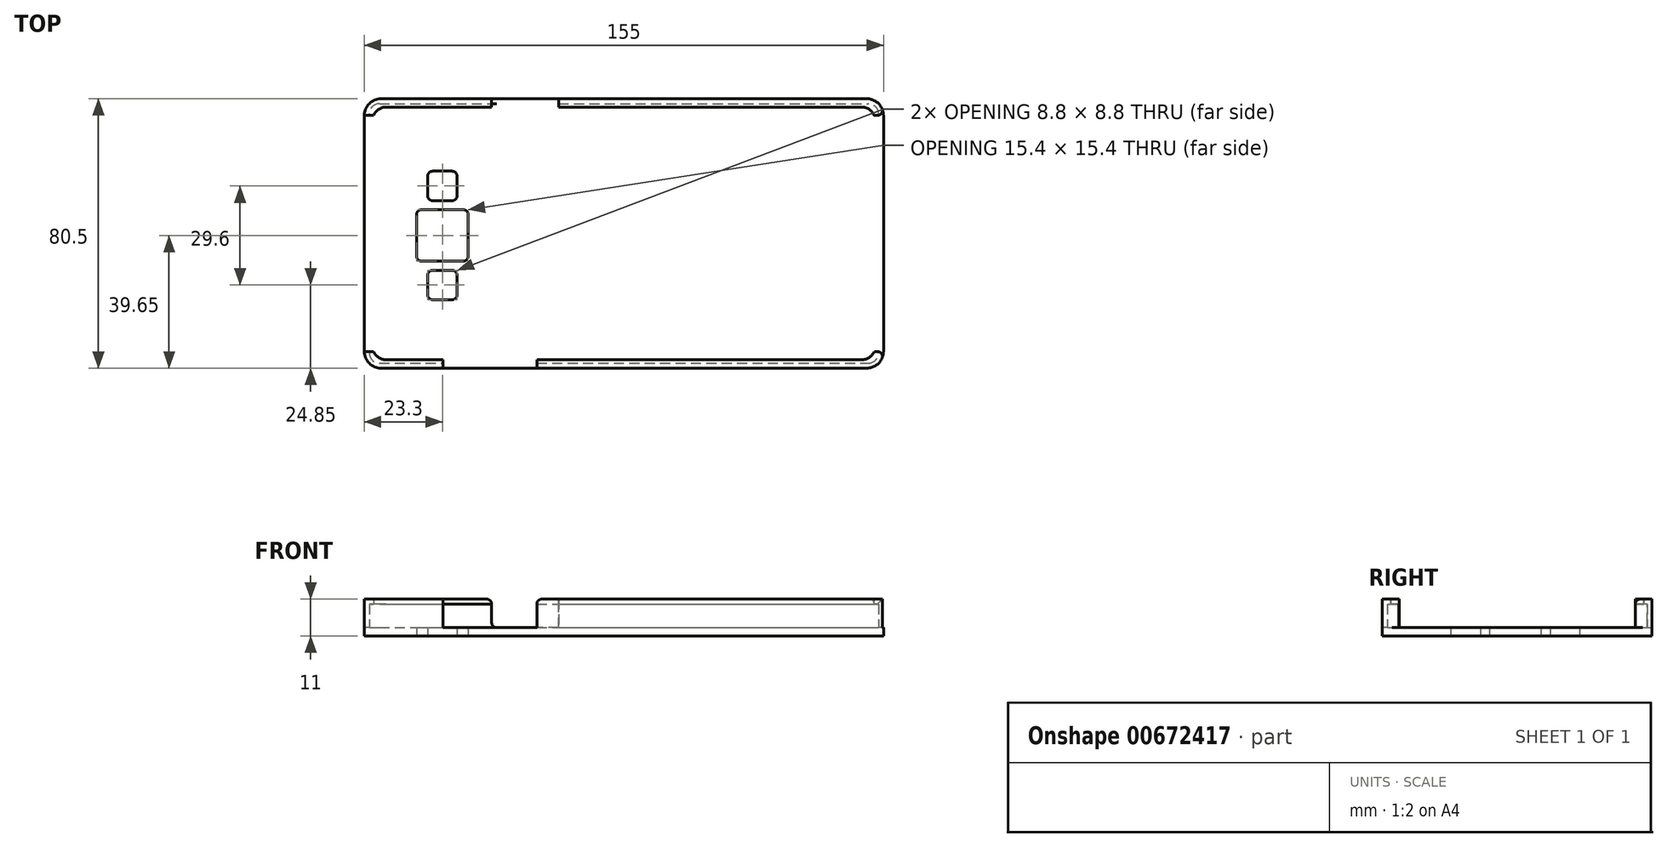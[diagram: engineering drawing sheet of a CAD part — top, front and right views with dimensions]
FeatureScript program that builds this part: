
annotation { "Feature Type Name" : "Feature", "Feature Type Description" : "" }
export const myFeature = defineFeature(function(context is Context, id is Id, definition is map)
    precondition{}
    {
        {
            var Q0;
            Q0=qCreatedBy(makeId("Top.planeOp"),FACE);
            var sketch = newSketch(context, id + "F0", { "sketchPlane" : qUnion([Q0])});
            skLineSegment(sketch, "E0.bottom", {"start": v(0, 0) * mm, "end": v(155, 0) * mm});
            skLineSegment(sketch, "E0.top", {"start": v(0, 80.5) * mm, "end": v(155, 80.5) * mm});
            skLineSegment(sketch, "E0.left", {"start": v(0, 0) * mm, "end": v(0, 80.5) * mm});
            skLineSegment(sketch, "E0.right", {"start": v(155, 0) * mm, "end": v(155, 80.5) * mm});
            skSolve(sketch);
        }
        {
            var Q0;
            Q0=qSketchRegion(id+"F0",true);
            extrude(context, id + "F1", {"entities" : qUnion([Q0]), "depth" : 9.5 * mm, "offsetDistance" : 25 * mm});
        }
        {
            var Q0;
            Q0=makeQuery(id+"F1.opExtrude","CAP_FACE",FACE,{"disambiguationData":[OSD([sQuery(id+"F0.wireOp",EDGE,"E0.bottom"),sQuery(id+"F0.wireOp",EDGE,"E0.top"),sQuery(id+"F0.wireOp",EDGE,"E0.left"),sQuery(id+"F0.wireOp",EDGE,"E0.right")])],"isStart":false});
            shell(context, id + "F2", {"entities" : qUnion([Q0]), "thickness" : 1.5 * mm});
        }
        {
            var Q0;
            Q0=makeQuery(id+"F1.opExtrude","CAP_FACE",FACE,{"disambiguationData":[OSD([sQuery(id+"F0.wireOp",EDGE,"E0.bottom"),sQuery(id+"F0.wireOp",EDGE,"E0.top"),sQuery(id+"F0.wireOp",EDGE,"E0.left"),sQuery(id+"F0.wireOp",EDGE,"E0.right")])],"isStart":false});
            var sketch = newSketch(context, id + "F3", { "sketchPlane" : qUnion([Q0])});
            skLineSegment(sketch, "E1.0", {"start": v(2.5, 78) * mm, "end": v(152.5, 78) * mm});
            skLineSegment(sketch, "E1.1", {"start": v(2.5, 2.5) * mm, "end": v(2.5, 78) * mm});
            skLineSegment(sketch, "E1.2", {"start": v(2.5, 2.5) * mm, "end": v(152.5, 2.5) * mm});
            skLineSegment(sketch, "E1.3", {"start": v(152.5, 2.5) * mm, "end": v(152.5, 78) * mm});
            skSolve(sketch);
        }
        {
            var Q0;
            Q0=makeQuery(id+"F3.imprint","IMPRINT",FACE,{"disambiguationData":[TD([[makeQuery(id+"F3.imprint","IMPRINT",EDGE,{"derivedFrom":sQuery(id+"F3.wireOp",EDGE,"E1.0")}),1.0]])]});
            var Q1;
            {var subQ6=sQuery(id+"F0.wireOp",EDGE,"E0.bottom");var subQ7=makeQuery(id+"F1.opExtrude","CAP_EDGE",EDGE,{"disambiguationData":[OSD([subQ6])],"isStart":false});Q1=makeQuery(id+"F3.imprint","IMPRINT",FACE,{"disambiguationData":[TD([[makeQuery(id+"F3.imprint","IMPRINT",EDGE,{"derivedFrom":subQ7}),1.0]])]});}
            extrude(context, id + "F4", {"entities" : qUnion([Q0, Q1]), "operationType" : NewBodyOperationType.ADD, "depth" : 1.5 * mm, "offsetDistance" : 25 * mm});
        }
        {
            var Q0;
            Q0=makeQuery(id+"F1.opExtrude","CAP_FACE",FACE,{"disambiguationData":[OSD([sQuery(id+"F0.wireOp",EDGE,"E0.bottom"),sQuery(id+"F0.wireOp",EDGE,"E0.top"),sQuery(id+"F0.wireOp",EDGE,"E0.left"),sQuery(id+"F0.wireOp",EDGE,"E0.right")])],"isStart":true});
            var sketch = newSketch(context, id + "F5", { "sketchPlane" : qUnion([Q0])});
            skLineSegment(sketch, "E2.bottom", {"start": v(18.9, -20.45) * mm, "end": v(27.7, -20.45) * mm});
            skLineSegment(sketch, "E2.top", {"start": v(18.9, -29.25) * mm, "end": v(27.7, -29.25) * mm});
            skLineSegment(sketch, "E2.left", {"start": v(18.9, -20.45) * mm, "end": v(18.9, -29.25) * mm});
            skLineSegment(sketch, "E2.right", {"start": v(27.7, -20.45) * mm, "end": v(27.7, -29.25) * mm});
            skLineSegment(sketch, "E3.bottom", {"start": v(15.6, -31.95) * mm, "end": v(31, -31.95) * mm});
            skLineSegment(sketch, "E3.top", {"start": v(15.6, -47.35) * mm, "end": v(31, -47.35) * mm});
            skLineSegment(sketch, "E3.left", {"start": v(15.6, -31.95) * mm, "end": v(15.6, -47.35) * mm});
            skLineSegment(sketch, "E3.right", {"start": v(31, -31.95) * mm, "end": v(31, -47.35) * mm});
            skLineSegment(sketch, "E4.bottom", {"start": v(18.9, -50.05) * mm, "end": v(27.7, -50.05) * mm});
            skLineSegment(sketch, "E4.top", {"start": v(18.9, -58.85) * mm, "end": v(27.7, -58.85) * mm});
            skLineSegment(sketch, "E4.left", {"start": v(18.9, -50.05) * mm, "end": v(18.9, -58.85) * mm});
            skLineSegment(sketch, "E4.right", {"start": v(27.7, -50.05) * mm, "end": v(27.7, -58.85) * mm});
            skLineSegment(sketch, "E5", {"start": v(12.52, -39.65) * mm, "end": v(41, -39.65) * mm});
            skPoint(sketch, "E5.startSnap0", {"position": v(15.6, -39.65) * mm});
            skLineSegment(sketch, "E6", {"start": v(16.62, -24.85) * mm, "end": v(34.64, -24.85) * mm});
            skPoint(sketch, "E6.startSnap0", {"position": v(18.9, -24.85) * mm});
            skLineSegment(sketch, "E7", {"start": v(16.41, -54.45) * mm, "end": v(34.85, -54.45) * mm});
            skPoint(sketch, "E7.startSnap0", {"position": v(18.9, -54.45) * mm});
            skSolve(sketch);
        }
        {
            var Q0;
            {var subQ0=sQuery(id+"F5.wireOp",EDGE,"E2.top");Q0=makeQuery(id+"F5.imprint","IMPRINT",FACE,{"disambiguationData":[TD([[makeQuery(id+"F5.imprint","IMPRINT",EDGE,{"derivedFrom":subQ0}),1.0]])]});}
            var Q1;
            {var subQ0=sQuery(id+"F5.wireOp",EDGE,"E2.bottom");Q1=makeQuery(id+"F5.imprint","IMPRINT",FACE,{"disambiguationData":[TD([[makeQuery(id+"F5.imprint","IMPRINT",EDGE,{"derivedFrom":subQ0}),-1.0]])]});}
            var Q2;
            {var subQ0=sQuery(id+"F5.wireOp",EDGE,"E3.bottom");Q2=makeQuery(id+"F5.imprint","IMPRINT",FACE,{"disambiguationData":[TD([[makeQuery(id+"F5.imprint","IMPRINT",EDGE,{"derivedFrom":subQ0}),-1.0]])]});}
            var Q3;
            {var subQ0=sQuery(id+"F5.wireOp",EDGE,"E3.top");Q3=makeQuery(id+"F5.imprint","IMPRINT",FACE,{"disambiguationData":[TD([[makeQuery(id+"F5.imprint","IMPRINT",EDGE,{"derivedFrom":subQ0}),1.0]])]});}
            var Q4;
            {var subQ0=sQuery(id+"F5.wireOp",EDGE,"E4.bottom");Q4=makeQuery(id+"F5.imprint","IMPRINT",FACE,{"disambiguationData":[TD([[makeQuery(id+"F5.imprint","IMPRINT",EDGE,{"derivedFrom":subQ0}),-1.0]])]});}
            var Q5;
            {var subQ0=sQuery(id+"F5.wireOp",EDGE,"E4.top");Q5=makeQuery(id+"F5.imprint","IMPRINT",FACE,{"disambiguationData":[TD([[makeQuery(id+"F5.imprint","IMPRINT",EDGE,{"derivedFrom":subQ0}),1.0]])]});}
            extrude(context, id + "F6", {"entities" : qUnion([Q0, Q1, Q2, Q3, Q4, Q5]), "operationType" : NewBodyOperationType.REMOVE, "endBound" : BoundingType.UP_TO_NEXT, "oppositeDirection" : true, "depth" : 25 * mm, "offsetDistance" : 25 * mm});
        }
        {
            var Q0;
            {var subQ0=sQuery(id+"F0.wireOp",EDGE,"E0.left");var subQ1=sQuery(id+"F0.wireOp",EDGE,"E0.bottom");Q0=makeQuery(id+"F4.boolean.opBoolean","MERGE",EDGE,{"derivedFrom":[makeQuery(id+"F1.opExtrude","SWEPT_EDGE",EDGE,{"disambiguationData":[OSD([subQ1,subQ0])]}),makeQuery(id+"F4.opExtrude","SWEPT_EDGE",EDGE,{"disambiguationData":[OSD([subQ1,subQ0])]})]});}
            var Q1;
            {var subQ0=sQuery(id+"F0.wireOp",EDGE,"E0.left");var subQ1=sQuery(id+"F0.wireOp",EDGE,"E0.top");Q1=makeQuery(id+"F4.boolean.opBoolean","MERGE",EDGE,{"derivedFrom":[makeQuery(id+"F1.opExtrude","SWEPT_EDGE",EDGE,{"disambiguationData":[OSD([subQ1,subQ0])]}),makeQuery(id+"F4.opExtrude","SWEPT_EDGE",EDGE,{"disambiguationData":[OSD([subQ1,subQ0])]})]});}
            var Q2;
            {var subQ0=sQuery(id+"F0.wireOp",EDGE,"E0.right");var subQ1=sQuery(id+"F0.wireOp",EDGE,"E0.bottom");Q2=makeQuery(id+"F4.boolean.opBoolean","MERGE",EDGE,{"derivedFrom":[makeQuery(id+"F1.opExtrude","SWEPT_EDGE",EDGE,{"disambiguationData":[OSD([subQ1,subQ0])]}),makeQuery(id+"F4.opExtrude","SWEPT_EDGE",EDGE,{"disambiguationData":[OSD([subQ1,subQ0])]})]});}
            var Q3;
            {var subQ0=sQuery(id+"F0.wireOp",EDGE,"E0.right");var subQ1=sQuery(id+"F0.wireOp",EDGE,"E0.top");Q3=makeQuery(id+"F4.boolean.opBoolean","MERGE",EDGE,{"derivedFrom":[makeQuery(id+"F1.opExtrude","SWEPT_EDGE",EDGE,{"disambiguationData":[OSD([subQ1,subQ0])]}),makeQuery(id+"F4.opExtrude","SWEPT_EDGE",EDGE,{"disambiguationData":[OSD([subQ1,subQ0])]})]});}
            fillet(context, id + "F7", {"entities" : qUnion([Q0, Q1, Q2, Q3]), "radius" : 5 * mm, "tangentPropagation" : true, "allowEdgeOverflow" : false});
        }
        {
            var Q0;
            Q0=makeQuery(id+"F2.opShell","OFFSET_EDGE",EDGE,{"disambiguationData":[OSD([sQuery(id+"F0.wireOp",EDGE,"E0.top"),sQuery(id+"F0.wireOp",EDGE,"E0.left")])]});
            var Q1;
            Q1=makeQuery(id+"F2.opShell","OFFSET_EDGE",EDGE,{"disambiguationData":[OSD([sQuery(id+"F0.wireOp",EDGE,"E0.bottom"),sQuery(id+"F0.wireOp",EDGE,"E0.left")])]});
            var Q2;
            Q2=makeQuery(id+"F2.opShell","OFFSET_EDGE",EDGE,{"disambiguationData":[OSD([sQuery(id+"F0.wireOp",EDGE,"E0.top"),sQuery(id+"F0.wireOp",EDGE,"E0.right")])]});
            var Q3;
            Q3=makeQuery(id+"F2.opShell","OFFSET_EDGE",EDGE,{"disambiguationData":[OSD([sQuery(id+"F0.wireOp",EDGE,"E0.bottom"),sQuery(id+"F0.wireOp",EDGE,"E0.right")])]});
            fillet(context, id + "F8", {"entities" : qUnion([Q0, Q1, Q2, Q3]), "radius" : 3 * mm, "tangentPropagation" : true, "allowEdgeOverflow" : false});
        }
        {
            var Q0;
            Q0=makeQuery(id+"F4.opExtrude","SWEPT_EDGE",EDGE,{"disambiguationData":[OSD([sQuery(id+"F3.wireOp",EDGE,"E1.0"),sQuery(id+"F3.wireOp",EDGE,"E1.1")])]});
            var Q1;
            Q1=makeQuery(id+"F4.opExtrude","SWEPT_EDGE",EDGE,{"disambiguationData":[OSD([sQuery(id+"F3.wireOp",EDGE,"E1.1"),sQuery(id+"F3.wireOp",EDGE,"E1.2")])]});
            var Q2;
            Q2=makeQuery(id+"F4.opExtrude","SWEPT_EDGE",EDGE,{"disambiguationData":[OSD([sQuery(id+"F3.wireOp",EDGE,"E1.0"),sQuery(id+"F3.wireOp",EDGE,"E1.3")])]});
            var Q3;
            Q3=makeQuery(id+"F4.opExtrude","SWEPT_EDGE",EDGE,{"disambiguationData":[OSD([sQuery(id+"F3.wireOp",EDGE,"E1.2"),sQuery(id+"F3.wireOp",EDGE,"E1.3")])]});
            fillet(context, id + "F9", {"entities" : qUnion([Q0, Q1, Q2, Q3]), "radius" : 4 * mm, "tangentPropagation" : true, "allowEdgeOverflow" : false});
        }
        {
            var Q0;
            {var subQ0=sQuery(id+"F0.wireOp",EDGE,"E0.left");Q0=makeQuery(id+"F4.boolean.opBoolean","MERGE",FACE,{"derivedFrom":[makeQuery(id+"F1.opExtrude","SWEPT_FACE",FACE,{"disambiguationData":[OSD([subQ0])]}),makeQuery(id+"F4.opExtrude","SWEPT_FACE",FACE,{"disambiguationData":[OSD([subQ0])]})]});}
            var sketch = newSketch(context, id + "F10", { "sketchPlane" : qUnion([Q0])});
            skLineSegment(sketch, "E8.bottom", {"start": v(-75.5, 11) * mm, "end": v(-5, 11) * mm});
            skLineSegment(sketch, "E8.top", {"start": v(-75.5, 1.5) * mm, "end": v(-5, 1.5) * mm});
            skLineSegment(sketch, "E8.left", {"start": v(-75.5, 11) * mm, "end": v(-75.5, 1.5) * mm});
            skLineSegment(sketch, "E8.right", {"start": v(-5, 11) * mm, "end": v(-5, 1.5) * mm});
            skSolve(sketch);
        }
        {
            var Q0;
            Q0=qSketchRegion(id+"F10",true);
            extrude(context, id + "F11", {"entities" : qUnion([Q0]), "operationType" : NewBodyOperationType.REMOVE, "endBound" : BoundingType.UP_TO_NEXT, "oppositeDirection" : true, "depth" : 25 * mm, "offsetDistance" : 25 * mm});
        }
        {
            var Q0;
            {var subQ0=sQuery(id+"F0.wireOp",EDGE,"E0.right");Q0=makeQuery(id+"F4.boolean.opBoolean","MERGE",FACE,{"derivedFrom":[makeQuery(id+"F1.opExtrude","SWEPT_FACE",FACE,{"disambiguationData":[OSD([subQ0])]}),makeQuery(id+"F4.opExtrude","SWEPT_FACE",FACE,{"disambiguationData":[OSD([subQ0])]})]});}
            var sketch = newSketch(context, id + "F12", { "sketchPlane" : qUnion([Q0])});
            skLineSegment(sketch, "E9.bottom", {"start": v(5, 11) * mm, "end": v(75.5, 11) * mm});
            skLineSegment(sketch, "E9.top", {"start": v(5, 1.5) * mm, "end": v(75.5, 1.5) * mm});
            skLineSegment(sketch, "E9.left", {"start": v(5, 11) * mm, "end": v(5, 1.5) * mm});
            skLineSegment(sketch, "E9.right", {"start": v(75.5, 11) * mm, "end": v(75.5, 1.5) * mm});
            skSolve(sketch);
        }
        {
            var Q0;
            Q0=makeQuery(id+"F12.imprint","IMPRINT",FACE,{"disambiguationData":[TD([[makeQuery(id+"F12.imprint","IMPRINT",EDGE,{"derivedFrom":sQuery(id+"F12.wireOp",EDGE,"E9.bottom")}),-1.0]])]});
            extrude(context, id + "F13", {"entities" : qUnion([Q0]), "operationType" : NewBodyOperationType.REMOVE, "endBound" : BoundingType.UP_TO_NEXT, "oppositeDirection" : true, "depth" : 25 * mm, "offsetDistance" : 25 * mm});
        }
        {
            var Q0;
            {var subQ0=sQuery(id+"F0.wireOp",EDGE,"E0.bottom");Q0=makeQuery(id+"F4.boolean.opBoolean","MERGE",FACE,{"derivedFrom":[makeQuery(id+"F1.opExtrude","SWEPT_FACE",FACE,{"disambiguationData":[OSD([subQ0])]}),makeQuery(id+"F4.opExtrude","SWEPT_FACE",FACE,{"disambiguationData":[OSD([subQ0])]})]});}
            var sketch = newSketch(context, id + "F14", { "sketchPlane" : qUnion([Q0])});
            skLineSegment(sketch, "E10.bottom", {"start": v(23.5, 11) * mm, "end": v(51.5, 11) * mm});
            skLineSegment(sketch, "E10.top", {"start": v(23.5, 1.5) * mm, "end": v(51.5, 1.5) * mm});
            skLineSegment(sketch, "E10.left", {"start": v(23.5, 11) * mm, "end": v(23.5, 1.5) * mm});
            skLineSegment(sketch, "E10.right", {"start": v(51.5, 11) * mm, "end": v(51.5, 1.5) * mm});
            skSolve(sketch);
        }
        {
            var Q0;
            Q0=makeQuery(id+"F14.imprint","IMPRINT",FACE,{"disambiguationData":[TD([[makeQuery(id+"F14.imprint","IMPRINT",EDGE,{"derivedFrom":sQuery(id+"F14.wireOp",EDGE,"E10.bottom")}),-1.0]])]});
            extrude(context, id + "F15", {"entities" : qUnion([Q0]), "operationType" : NewBodyOperationType.REMOVE, "endBound" : BoundingType.UP_TO_NEXT, "oppositeDirection" : true, "depth" : 25 * mm, "offsetDistance" : 25 * mm});
        }
        {
            var Q0;
            Q0=makeQuery(id+"F15.boolean.opBoolean","MERGE",FACE,{"derivedFrom":[makeQuery(id+"F13.boolean.opBoolean","MERGE",FACE,{"derivedFrom":[makeQuery(id+"F11.boolean.opBoolean","MERGE",FACE,{"derivedFrom":[makeQuery(id+"F2.opShell","OFFSET_FACE",FACE,{"disambiguationData":[OSD([sQuery(id+"F0.wireOp",EDGE,"E0.bottom"),sQuery(id+"F0.wireOp",EDGE,"E0.top"),sQuery(id+"F0.wireOp",EDGE,"E0.left"),sQuery(id+"F0.wireOp",EDGE,"E0.right")])]})],"fromTools":[makeQuery(id+"F11.opExtrude","SWEPT_FACE",FACE,{"disambiguationData":[OSD([sQuery(id+"F10.wireOp",EDGE,"E8.top")])]})]})],"fromTools":[makeQuery(id+"F13.opExtrude","SWEPT_FACE",FACE,{"disambiguationData":[OSD([sQuery(id+"F12.wireOp",EDGE,"E9.top")])]})]})],"fromTools":[makeQuery(id+"F15.opExtrude","SWEPT_FACE",FACE,{"disambiguationData":[OSD([sQuery(id+"F14.wireOp",EDGE,"E10.top")])]})]});
            extrude(context, id + "F16", {"entities" : qUnion([Q0]), "operationType" : NewBodyOperationType.ADD, "depth" : 1 * mm, "offsetDistance" : 25 * mm});
        }
        {
            var Q0;
            {var subQ0=sQuery(id+"F0.wireOp",EDGE,"E0.top");Q0=makeQuery(id+"F4.boolean.opBoolean","MERGE",FACE,{"derivedFrom":[makeQuery(id+"F1.opExtrude","SWEPT_FACE",FACE,{"disambiguationData":[OSD([subQ0])]}),makeQuery(id+"F4.opExtrude","SWEPT_FACE",FACE,{"disambiguationData":[OSD([subQ0])]})]});}
            var sketch = newSketch(context, id + "F17", { "sketchPlane" : qUnion([Q0])});
            skLineSegment(sketch, "E11.bottom", {"start": v(-58, 11) * mm, "end": v(-38, 11) * mm});
            skLineSegment(sketch, "E11.top", {"start": v(-58, 2.5) * mm, "end": v(-38, 2.5) * mm});
            skLineSegment(sketch, "E11.left", {"start": v(-58, 11) * mm, "end": v(-58, 2.5) * mm});
            skLineSegment(sketch, "E11.right", {"start": v(-38, 11) * mm, "end": v(-38, 2.5) * mm});
            skSolve(sketch);
        }
        {
            var Q0;
            Q0=makeQuery(id+"F17.imprint","IMPRINT",FACE,{"disambiguationData":[TD([[makeQuery(id+"F17.imprint","IMPRINT",EDGE,{"derivedFrom":sQuery(id+"F17.wireOp",EDGE,"E11.bottom")}),1.0]])]});
            extrude(context, id + "F18", {"entities" : qUnion([Q0]), "operationType" : NewBodyOperationType.REMOVE, "endBound" : BoundingType.UP_TO_NEXT, "oppositeDirection" : true, "depth" : 25 * mm, "offsetDistance" : 25 * mm});
        }
        {
            var Q0;
            Q0=makeQuery(id+"F18.boolean.opBoolean","COPY",EDGE,{"derivedFrom":makeQuery(id+"F18.opExtrude","SWEPT_EDGE",EDGE,{"disambiguationData":[OSD([sQuery(id+"F0.wireOp",EDGE,"E0.top"),sQuery(id+"F17.wireOp",EDGE,"E11.bottom"),sQuery(id+"F17.wireOp",EDGE,"E11.right")])]})});
            var Q1;
            Q1=makeQuery(id+"F18.boolean.opBoolean","COPY",EDGE,{"derivedFrom":makeQuery(id+"F18.opExtrude","SWEPT_EDGE",EDGE,{"disambiguationData":[OSD([sQuery(id+"F0.wireOp",EDGE,"E0.top"),sQuery(id+"F17.wireOp",EDGE,"E11.bottom"),sQuery(id+"F17.wireOp",EDGE,"E11.left")])]})});
            var Q2;
            Q2=makeQuery(id+"F18.boolean.opBoolean","COPY",EDGE,{"derivedFrom":makeQuery(id+"F18.opExtrude","CAP_EDGE",EDGE,{"disambiguationData":[OSD([sQuery(id+"F17.wireOp",EDGE,"E11.right")])],"isStart":true})});
            var Q3;
            Q3=makeQuery(id+"F18.boolean.opBoolean","COPY",EDGE,{"derivedFrom":makeQuery(id+"F18.opExtrude","CAP_EDGE",EDGE,{"disambiguationData":[OSD([sQuery(id+"F17.wireOp",EDGE,"E11.left")])],"isStart":true})});
            var Q4;
            Q4=makeQuery(id+"F18.boolean.opBoolean","COPY",EDGE,{"derivedFrom":makeQuery(id+"F18.opExtrude","SWEPT_EDGE",EDGE,{"disambiguationData":[OSD([sQuery(id+"F17.wireOp",EDGE,"E11.top"),sQuery(id+"F17.wireOp",EDGE,"E11.right")])]})});
            var Q5;
            Q5=makeQuery(id+"F15.boolean.opBoolean","COPY",EDGE,{"derivedFrom":makeQuery(id+"F15.opExtrude","SWEPT_EDGE",EDGE,{"disambiguationData":[OSD([sQuery(id+"F0.wireOp",EDGE,"E0.bottom"),sQuery(id+"F14.wireOp",EDGE,"E10.bottom"),sQuery(id+"F14.wireOp",EDGE,"E10.right")])]})});
            var Q6;
            Q6=makeQuery(id+"F16.opExtrude","CAP_EDGE",EDGE,{"disambiguationData":[OSD([sQuery(id+"F14.wireOp",EDGE,"E10.top"),sQuery(id+"F14.wireOp",EDGE,"E10.right")])],"isStart":false});
            var Q7;
            Q7=makeQuery(id+"F15.boolean.opBoolean","COPY",EDGE,{"derivedFrom":makeQuery(id+"F15.opExtrude","CAP_EDGE",EDGE,{"disambiguationData":[OSD([sQuery(id+"F14.wireOp",EDGE,"E10.right")])],"isStart":true})});
            var Q8;
            Q8=makeQuery(id+"F15.boolean.opBoolean","COPY",EDGE,{"derivedFrom":makeQuery(id+"F15.opExtrude","CAP_EDGE",EDGE,{"disambiguationData":[OSD([sQuery(id+"F14.wireOp",EDGE,"E10.left")])],"isStart":true})});
            var Q9;
            Q9=makeQuery(id+"F15.boolean.opBoolean","COPY",EDGE,{"derivedFrom":makeQuery(id+"F15.opExtrude","SWEPT_EDGE",EDGE,{"disambiguationData":[OSD([sQuery(id+"F0.wireOp",EDGE,"E0.bottom"),sQuery(id+"F14.wireOp",EDGE,"E10.bottom"),sQuery(id+"F14.wireOp",EDGE,"E10.left")])]})});
            var Q10;
            Q10=makeQuery(id+"F13.boolean.opBoolean","COPY",EDGE,{"derivedFrom":makeQuery(id+"F13.opExtrude","CAP_EDGE",EDGE,{"disambiguationData":[OSD([sQuery(id+"F12.wireOp",EDGE,"E9.right")]),topologyDisambiguationEdgeConnected([makeQuery(id+"F2.opShell","OFFSET_FACE",FACE,{"disambiguationData":[OSD([sQuery(id+"F0.wireOp",EDGE,"E0.right")])]})])],"isStart":false})});
            var Q11;
            Q11=makeQuery(id+"F13.boolean.opBoolean","COPY",EDGE,{"derivedFrom":makeQuery(id+"F13.opExtrude","SWEPT_EDGE",EDGE,{"disambiguationData":[OSD([sQuery(id+"F0.wireOp",EDGE,"E0.bottom"),sQuery(id+"F0.wireOp",EDGE,"E0.top"),sQuery(id+"F0.wireOp",EDGE,"E0.left"),sQuery(id+"F0.wireOp",EDGE,"E0.right"),sQuery(id+"F3.wireOp",EDGE,"E1.0"),sQuery(id+"F3.wireOp",EDGE,"E1.1"),sQuery(id+"F3.wireOp",EDGE,"E1.2"),sQuery(id+"F3.wireOp",EDGE,"E1.3"),sQuery(id+"F12.wireOp",EDGE,"E9.bottom"),sQuery(id+"F12.wireOp",EDGE,"E9.left")])]})});
            var Q12;
            {var subQ0=sQuery(id+"F0.wireOp",EDGE,"E0.right");var subQ1=sQuery(id+"F0.wireOp",EDGE,"E0.top");Q12=makeQuery(id+"F16.boolean.opBoolean","SPLIT",EDGE,{"derivedFrom":makeQuery(id+"F13.boolean.opBoolean","MERGE",EDGE,{"derivedFrom":[makeQuery(id+"F7.opFillet","BLEND_EDGE",EDGE,{"blendedFrom":[makeQuery(id+"F4.boolean.opBoolean","MERGE",EDGE,{"derivedFrom":[makeQuery(id+"F1.opExtrude","SWEPT_EDGE",EDGE,{"disambiguationData":[OSD([subQ1,subQ0])]}),makeQuery(id+"F4.opExtrude","SWEPT_EDGE",EDGE,{"disambiguationData":[OSD([subQ1,subQ0])]})]}),makeQuery(id+"F4.boolean.opBoolean","MERGE",FACE,{"derivedFrom":[makeQuery(id+"F1.opExtrude","SWEPT_FACE",FACE,{"disambiguationData":[OSD([subQ0])]}),makeQuery(id+"F4.opExtrude","SWEPT_FACE",FACE,{"disambiguationData":[OSD([subQ0])]})]})],"blendedInto":[makeQuery(id+"F4.boolean.opBoolean","MERGE",FACE,{"derivedFrom":[makeQuery(id+"F1.opExtrude","SWEPT_FACE",FACE,{"disambiguationData":[OSD([subQ0])]}),makeQuery(id+"F4.opExtrude","SWEPT_FACE",FACE,{"disambiguationData":[OSD([subQ0])]})]})]})],"fromTools":[makeQuery(id+"F13.opExtrude","CAP_EDGE",EDGE,{"disambiguationData":[OSD([subQ1,subQ0,sQuery(id+"F12.wireOp",EDGE,"E9.right")])],"isStart":true})]})});}
            var Q13;
            Q13=makeQuery(id+"F13.boolean.opBoolean","COPY",EDGE,{"derivedFrom":makeQuery(id+"F13.opExtrude","SWEPT_EDGE",EDGE,{"disambiguationData":[OSD([sQuery(id+"F0.wireOp",EDGE,"E0.bottom"),sQuery(id+"F0.wireOp",EDGE,"E0.top"),sQuery(id+"F0.wireOp",EDGE,"E0.left"),sQuery(id+"F0.wireOp",EDGE,"E0.right"),sQuery(id+"F3.wireOp",EDGE,"E1.0"),sQuery(id+"F3.wireOp",EDGE,"E1.1"),sQuery(id+"F3.wireOp",EDGE,"E1.2"),sQuery(id+"F3.wireOp",EDGE,"E1.3"),sQuery(id+"F12.wireOp",EDGE,"E9.bottom"),sQuery(id+"F12.wireOp",EDGE,"E9.right")])]})});
            var Q14;
            {var subQ0=sQuery(id+"F0.wireOp",EDGE,"E0.right");var subQ1=sQuery(id+"F0.wireOp",EDGE,"E0.bottom");Q14=makeQuery(id+"F16.boolean.opBoolean","SPLIT",EDGE,{"derivedFrom":makeQuery(id+"F13.boolean.opBoolean","MERGE",EDGE,{"derivedFrom":[makeQuery(id+"F7.opFillet","BLEND_EDGE",EDGE,{"blendedFrom":[makeQuery(id+"F4.boolean.opBoolean","MERGE",EDGE,{"derivedFrom":[makeQuery(id+"F1.opExtrude","SWEPT_EDGE",EDGE,{"disambiguationData":[OSD([subQ1,subQ0])]}),makeQuery(id+"F4.opExtrude","SWEPT_EDGE",EDGE,{"disambiguationData":[OSD([subQ1,subQ0])]})]}),makeQuery(id+"F4.boolean.opBoolean","MERGE",FACE,{"derivedFrom":[makeQuery(id+"F1.opExtrude","SWEPT_FACE",FACE,{"disambiguationData":[OSD([subQ0])]}),makeQuery(id+"F4.opExtrude","SWEPT_FACE",FACE,{"disambiguationData":[OSD([subQ0])]})]})],"blendedInto":[makeQuery(id+"F4.boolean.opBoolean","MERGE",FACE,{"derivedFrom":[makeQuery(id+"F1.opExtrude","SWEPT_FACE",FACE,{"disambiguationData":[OSD([subQ0])]}),makeQuery(id+"F4.opExtrude","SWEPT_FACE",FACE,{"disambiguationData":[OSD([subQ0])]})]})]})],"fromTools":[makeQuery(id+"F13.opExtrude","CAP_EDGE",EDGE,{"disambiguationData":[OSD([subQ1,subQ0,sQuery(id+"F12.wireOp",EDGE,"E9.left")])],"isStart":true})]})});}
            var Q15;
            Q15=makeQuery(id+"F11.boolean.opBoolean","COPY",EDGE,{"derivedFrom":makeQuery(id+"F11.opExtrude","SWEPT_EDGE",EDGE,{"disambiguationData":[OSD([sQuery(id+"F0.wireOp",EDGE,"E0.bottom"),sQuery(id+"F0.wireOp",EDGE,"E0.top"),sQuery(id+"F0.wireOp",EDGE,"E0.left"),sQuery(id+"F0.wireOp",EDGE,"E0.right"),sQuery(id+"F3.wireOp",EDGE,"E1.0"),sQuery(id+"F3.wireOp",EDGE,"E1.1"),sQuery(id+"F3.wireOp",EDGE,"E1.2"),sQuery(id+"F3.wireOp",EDGE,"E1.3"),sQuery(id+"F10.wireOp",EDGE,"E8.bottom"),sQuery(id+"F10.wireOp",EDGE,"E8.left")])]})});
            var Q16;
            Q16=makeQuery(id+"F11.boolean.opBoolean","COPY",EDGE,{"derivedFrom":makeQuery(id+"F11.opExtrude","SWEPT_EDGE",EDGE,{"disambiguationData":[OSD([sQuery(id+"F0.wireOp",EDGE,"E0.bottom"),sQuery(id+"F0.wireOp",EDGE,"E0.top"),sQuery(id+"F0.wireOp",EDGE,"E0.left"),sQuery(id+"F0.wireOp",EDGE,"E0.right"),sQuery(id+"F3.wireOp",EDGE,"E1.0"),sQuery(id+"F3.wireOp",EDGE,"E1.1"),sQuery(id+"F3.wireOp",EDGE,"E1.2"),sQuery(id+"F3.wireOp",EDGE,"E1.3"),sQuery(id+"F10.wireOp",EDGE,"E8.bottom"),sQuery(id+"F10.wireOp",EDGE,"E8.right")])]})});
            fillet(context, id + "F19", {"entities" : qUnion([Q0, Q1, Q2, Q3, Q4, Q5, Q6, Q7, Q8, Q9, Q10, Q11, Q12, Q13, Q14, Q15, Q16]), "radius" : 1.5 * mm, "tangentPropagation" : true, "allowEdgeOverflow" : false});
        }
        {
            var Q0;
            {var subQ0=sQuery(id+"F5.wireOp",EDGE,"E4.right");var subQ1=sQuery(id+"F5.wireOp",EDGE,"E4.top");Q0=makeQuery(id+"F16.boolean.opBoolean","MERGE",EDGE,{"derivedFrom":[makeQuery(id+"F6.boolean.opBoolean","COPY",EDGE,{"derivedFrom":makeQuery(id+"F6.opExtrude","SWEPT_EDGE",EDGE,{"disambiguationData":[OSD([subQ1,subQ0])]})}),makeQuery(id+"F16.opExtrude","SWEPT_EDGE",EDGE,{"disambiguationData":[OSD([subQ1,subQ0])]})]});}
            var Q1;
            {var subQ0=sQuery(id+"F5.wireOp",EDGE,"E4.left");var subQ1=sQuery(id+"F5.wireOp",EDGE,"E4.top");Q1=makeQuery(id+"F16.boolean.opBoolean","MERGE",EDGE,{"derivedFrom":[makeQuery(id+"F6.boolean.opBoolean","COPY",EDGE,{"derivedFrom":makeQuery(id+"F6.opExtrude","SWEPT_EDGE",EDGE,{"disambiguationData":[OSD([subQ1,subQ0])]})}),makeQuery(id+"F16.opExtrude","SWEPT_EDGE",EDGE,{"disambiguationData":[OSD([subQ1,subQ0])]})]});}
            var Q2;
            {var subQ0=sQuery(id+"F5.wireOp",EDGE,"E4.left");var subQ1=sQuery(id+"F5.wireOp",EDGE,"E4.bottom");Q2=makeQuery(id+"F16.boolean.opBoolean","MERGE",EDGE,{"derivedFrom":[makeQuery(id+"F6.boolean.opBoolean","COPY",EDGE,{"derivedFrom":makeQuery(id+"F6.opExtrude","SWEPT_EDGE",EDGE,{"disambiguationData":[OSD([subQ1,subQ0])]})}),makeQuery(id+"F16.opExtrude","SWEPT_EDGE",EDGE,{"disambiguationData":[OSD([subQ1,subQ0])]})]});}
            var Q3;
            {var subQ0=sQuery(id+"F5.wireOp",EDGE,"E4.right");var subQ1=sQuery(id+"F5.wireOp",EDGE,"E4.bottom");Q3=makeQuery(id+"F16.boolean.opBoolean","MERGE",EDGE,{"derivedFrom":[makeQuery(id+"F6.boolean.opBoolean","COPY",EDGE,{"derivedFrom":makeQuery(id+"F6.opExtrude","SWEPT_EDGE",EDGE,{"disambiguationData":[OSD([subQ1,subQ0])]})}),makeQuery(id+"F16.opExtrude","SWEPT_EDGE",EDGE,{"disambiguationData":[OSD([subQ1,subQ0])]})]});}
            var Q4;
            {var subQ0=sQuery(id+"F5.wireOp",EDGE,"E3.right");var subQ1=sQuery(id+"F5.wireOp",EDGE,"E3.top");Q4=makeQuery(id+"F16.boolean.opBoolean","MERGE",EDGE,{"derivedFrom":[makeQuery(id+"F6.boolean.opBoolean","COPY",EDGE,{"derivedFrom":makeQuery(id+"F6.opExtrude","SWEPT_EDGE",EDGE,{"disambiguationData":[OSD([subQ1,subQ0])]})}),makeQuery(id+"F16.opExtrude","SWEPT_EDGE",EDGE,{"disambiguationData":[OSD([subQ1,subQ0])]})]});}
            var Q5;
            {var subQ0=sQuery(id+"F5.wireOp",EDGE,"E3.right");var subQ1=sQuery(id+"F5.wireOp",EDGE,"E3.bottom");Q5=makeQuery(id+"F16.boolean.opBoolean","MERGE",EDGE,{"derivedFrom":[makeQuery(id+"F6.boolean.opBoolean","COPY",EDGE,{"derivedFrom":makeQuery(id+"F6.opExtrude","SWEPT_EDGE",EDGE,{"disambiguationData":[OSD([subQ1,subQ0])]})}),makeQuery(id+"F16.opExtrude","SWEPT_EDGE",EDGE,{"disambiguationData":[OSD([subQ1,subQ0])]})]});}
            var Q6;
            {var subQ0=sQuery(id+"F5.wireOp",EDGE,"E3.left");var subQ1=sQuery(id+"F5.wireOp",EDGE,"E3.top");Q6=makeQuery(id+"F16.boolean.opBoolean","MERGE",EDGE,{"derivedFrom":[makeQuery(id+"F6.boolean.opBoolean","COPY",EDGE,{"derivedFrom":makeQuery(id+"F6.opExtrude","SWEPT_EDGE",EDGE,{"disambiguationData":[OSD([subQ1,subQ0])]})}),makeQuery(id+"F16.opExtrude","SWEPT_EDGE",EDGE,{"disambiguationData":[OSD([subQ1,subQ0])]})]});}
            var Q7;
            {var subQ0=sQuery(id+"F5.wireOp",EDGE,"E3.left");var subQ1=sQuery(id+"F5.wireOp",EDGE,"E3.bottom");Q7=makeQuery(id+"F16.boolean.opBoolean","MERGE",EDGE,{"derivedFrom":[makeQuery(id+"F6.boolean.opBoolean","COPY",EDGE,{"derivedFrom":makeQuery(id+"F6.opExtrude","SWEPT_EDGE",EDGE,{"disambiguationData":[OSD([subQ1,subQ0])]})}),makeQuery(id+"F16.opExtrude","SWEPT_EDGE",EDGE,{"disambiguationData":[OSD([subQ1,subQ0])]})]});}
            var Q8;
            {var subQ0=sQuery(id+"F5.wireOp",EDGE,"E2.left");var subQ1=sQuery(id+"F5.wireOp",EDGE,"E2.bottom");Q8=makeQuery(id+"F16.boolean.opBoolean","MERGE",EDGE,{"derivedFrom":[makeQuery(id+"F6.boolean.opBoolean","COPY",EDGE,{"derivedFrom":makeQuery(id+"F6.opExtrude","SWEPT_EDGE",EDGE,{"disambiguationData":[OSD([subQ1,subQ0])]})}),makeQuery(id+"F16.opExtrude","SWEPT_EDGE",EDGE,{"disambiguationData":[OSD([subQ1,subQ0])]})]});}
            var Q9;
            {var subQ0=sQuery(id+"F5.wireOp",EDGE,"E2.right");var subQ1=sQuery(id+"F5.wireOp",EDGE,"E2.bottom");Q9=makeQuery(id+"F16.boolean.opBoolean","MERGE",EDGE,{"derivedFrom":[makeQuery(id+"F6.boolean.opBoolean","COPY",EDGE,{"derivedFrom":makeQuery(id+"F6.opExtrude","SWEPT_EDGE",EDGE,{"disambiguationData":[OSD([subQ1,subQ0])]})}),makeQuery(id+"F16.opExtrude","SWEPT_EDGE",EDGE,{"disambiguationData":[OSD([subQ1,subQ0])]})]});}
            var Q10;
            {var subQ0=sQuery(id+"F5.wireOp",EDGE,"E2.right");var subQ1=sQuery(id+"F5.wireOp",EDGE,"E2.top");Q10=makeQuery(id+"F16.boolean.opBoolean","MERGE",EDGE,{"derivedFrom":[makeQuery(id+"F6.boolean.opBoolean","COPY",EDGE,{"derivedFrom":makeQuery(id+"F6.opExtrude","SWEPT_EDGE",EDGE,{"disambiguationData":[OSD([subQ1,subQ0])]})}),makeQuery(id+"F16.opExtrude","SWEPT_EDGE",EDGE,{"disambiguationData":[OSD([subQ1,subQ0])]})]});}
            var Q11;
            {var subQ0=sQuery(id+"F5.wireOp",EDGE,"E2.left");var subQ1=sQuery(id+"F5.wireOp",EDGE,"E2.top");Q11=makeQuery(id+"F16.boolean.opBoolean","MERGE",EDGE,{"derivedFrom":[makeQuery(id+"F6.boolean.opBoolean","COPY",EDGE,{"derivedFrom":makeQuery(id+"F6.opExtrude","SWEPT_EDGE",EDGE,{"disambiguationData":[OSD([subQ1,subQ0])]})}),makeQuery(id+"F16.opExtrude","SWEPT_EDGE",EDGE,{"disambiguationData":[OSD([subQ1,subQ0])]})]});}
            fillet(context, id + "F20", {"entities" : qUnion([Q0, Q1, Q2, Q3, Q4, Q5, Q6, Q7, Q8, Q9, Q10, Q11]), "radius" : 1.5 * mm, "tangentPropagation" : true, "allowEdgeOverflow" : false});
        }
    });
